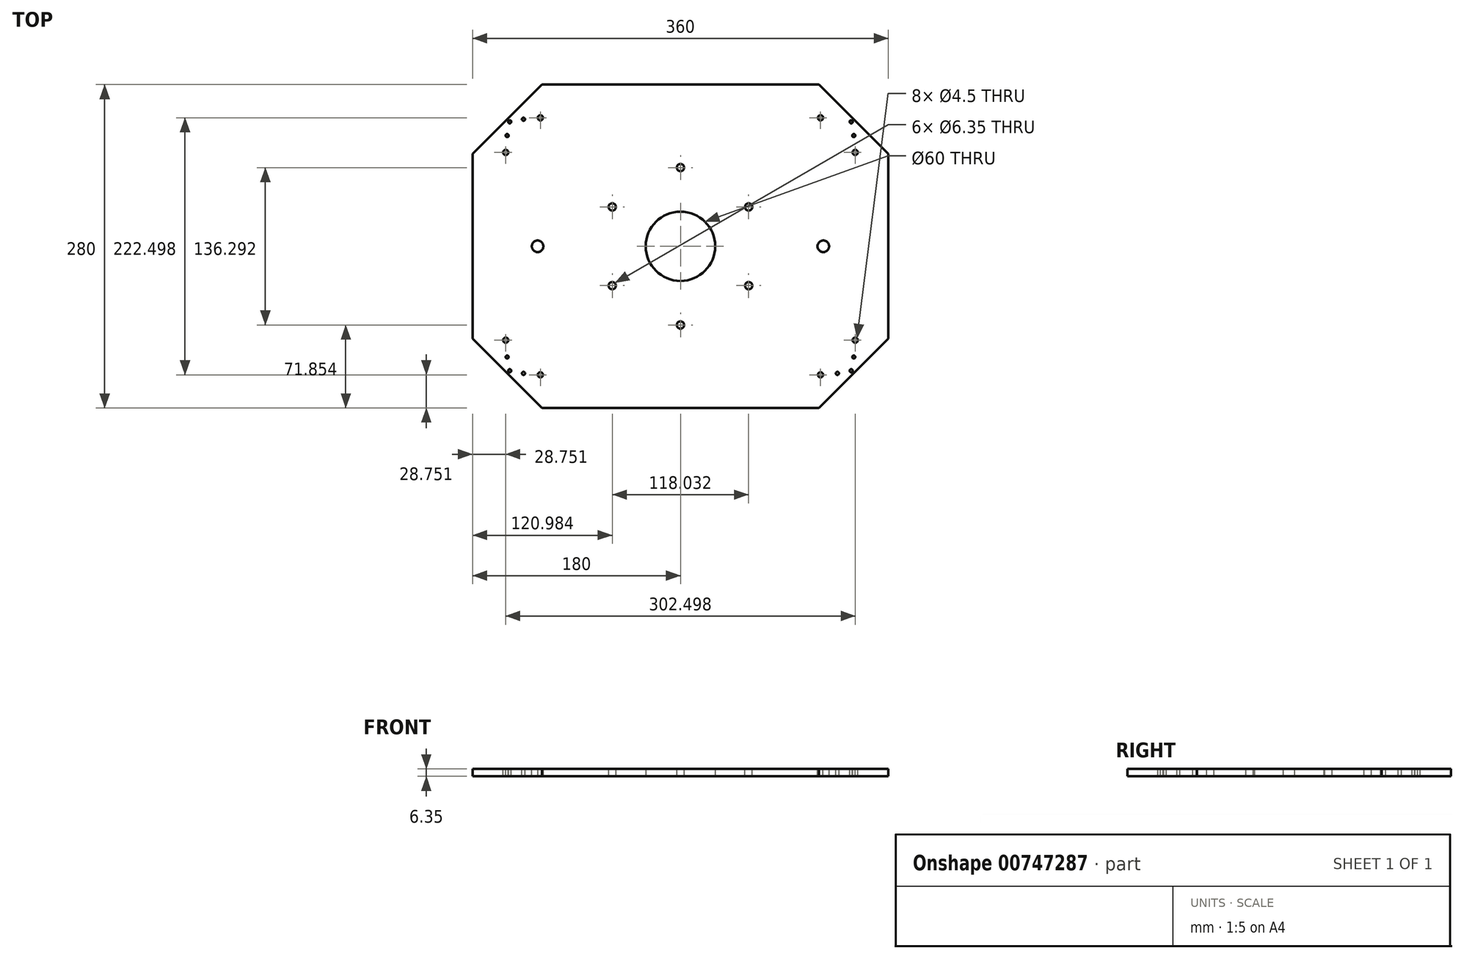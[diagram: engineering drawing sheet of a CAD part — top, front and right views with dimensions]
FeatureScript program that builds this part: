
annotation { "Feature Type Name" : "Feature", "Feature Type Description" : "" }
export const myFeature = defineFeature(function(context is Context, id is Id, definition is map)
    precondition{}
    {
        {
            var Q0;
            Q0=qCreatedBy(makeId("Top.planeOp"),FACE);
            var sketch = newSketch(context, id + "F0", { "sketchPlane" : qUnion([Q0])});
            skLineSegment(sketch, "E0", {"start": v(-120, 0) * mm, "end": v(-180, 60) * mm});
            skLineSegment(sketch, "E1", {"start": v(-180, 60) * mm, "end": v(-180, 220) * mm});
            skLineSegment(sketch, "E2", {"start": v(-180, 220) * mm, "end": v(-120, 280) * mm});
            skLineSegment(sketch, "E3", {"start": v(-120, 280) * mm, "end": v(120, 280) * mm});
            skLineSegment(sketch, "E4", {"start": v(120, 280) * mm, "end": v(180, 220) * mm});
            skLineSegment(sketch, "E5", {"start": v(180, 220) * mm, "end": v(180, 60) * mm});
            skLineSegment(sketch, "E6", {"start": v(180, 60) * mm, "end": v(120, 0) * mm});
            skLineSegment(sketch, "E7", {"start": v(120, 0) * mm, "end": v(-120, 0) * mm});
            skPoint(sketch, "E8.endSnap0", {"position": v(0, 280) * mm});
            skPoint(sketch, "E9.0.midPoint", {"position": v(0, 204.86) * mm});
            skPoint(sketch, "E10.0.midPoint", {"position": v(30.27, 157.38) * mm});
            skLineSegment(sketch, "E11", {"start": v(-180, 140) * mm, "end": v(180, 140) * mm, "construction": true});
            skLineSegment(sketch, "E12", {"start": v(0, 280) * mm, "end": v(0, 0) * mm, "construction": true});
            skCircle(sketch, "E13", {"center": v(0, 140) * mm, "radius": 30 * mm});
            skSolve(sketch);
        }
        {
            var Q0;
            Q0=qSketchRegion(id+"F0",true);
            extrude(context, id + "F1", {"entities" : qUnion([Q0]), "depth" : 6.35 * mm, "offsetDistance" : 25 * mm});
        }
        {
            var Q0;
            {var subQ0=sQuery(id+"F0.wireOp",EDGE,"E2");var subQ1=sQuery(id+"F0.wireOp",EDGE,"E1");var subQ2=sQuery(id+"F0.wireOp",EDGE,"E3");var subQ3=sQuery(id+"F0.wireOp",EDGE,"E0");var subQ4=sQuery(id+"F0.wireOp",EDGE,"E4");var subQ5=sQuery(id+"F0.wireOp",EDGE,"E5");var subQ6=sQuery(id+"F0.wireOp",EDGE,"E6");var subQ7=sQuery(id+"F0.wireOp",EDGE,"E7");Q0=makeQuery(id+"FAH0EIdtt6uSNSP_1.boolean.opBoolean","SPLIT",FACE,{"disambiguationData":[TD([makeQuery(id+"F1.opExtrude","SWEPT_FACE",FACE,{"disambiguationData":[OSD([subQ3])]})])],"derivedFrom":makeQuery(id+"F1.opExtrude","CAP_FACE",FACE,{"disambiguationData":[OSD([subQ3,subQ1,subQ0,subQ2,subQ4,subQ5,subQ6,subQ7,sQuery(id+"F0.wireOp",EDGE,"E10.0"),sQuery(id+"F0.wireOp",EDGE,"E10.1"),sQuery(id+"F0.wireOp",EDGE,"E10.2"),sQuery(id+"F0.wireOp",EDGE,"E10.3"),sQuery(id+"F0.wireOp",EDGE,"E10.4"),sQuery(id+"F0.wireOp",EDGE,"E10.5")])],"isStart":false})});}
            var sketch = newSketch(context, id + "F2", { "sketchPlane" : qUnion([Q0])});
            skLineSegment(sketch, "E14", {"start": v(-180, 140) * mm, "end": v(180, 140) * mm, "construction": true});
            skPoint(sketch, "E15", {"position": v(0, 140) * mm});
            skPoint(sketch, "E16", {"position": v(-123.65, 140) * mm});
            skPoint(sketch, "E17", {"position": v(123.65, 140) * mm});
            skSolve(sketch);
        }
        {
            var Q0;
            Q0=sQuery(id+"F2.wireOp",VERTEX,"E16");
            var Q1;
            Q1=sQuery(id+"F2.wireOp",VERTEX,"E17");
            var Q2;
            Q2=makeQuery(id+"F1.opExtrude","SWEPT_BODY",BODY,{"disambiguationData":[OSD([sQuery(id+"F0.wireOp",EDGE,"E0"),sQuery(id+"F0.wireOp",EDGE,"E1"),sQuery(id+"F0.wireOp",EDGE,"E2"),sQuery(id+"F0.wireOp",EDGE,"E3"),sQuery(id+"F0.wireOp",EDGE,"E4"),sQuery(id+"F0.wireOp",EDGE,"E5"),sQuery(id+"F0.wireOp",EDGE,"E6"),sQuery(id+"F0.wireOp",EDGE,"E7"),sQuery(id+"F0.wireOp",EDGE,"E10.0"),sQuery(id+"F0.wireOp",EDGE,"E10.1"),sQuery(id+"F0.wireOp",EDGE,"E10.2"),sQuery(id+"F0.wireOp",EDGE,"E10.3"),sQuery(id+"F0.wireOp",EDGE,"E10.4"),sQuery(id+"F0.wireOp",EDGE,"E10.5")])]});
            hole(context, id + "F3", {"style" : HoleStyle.SIMPLE, "endStyle" : HoleEndStyle.THROUGH, "holeDiameter" : 10 * mm, "majorDiameter" : 3.17 * mm, "isTappedThrough" : true, "tappedDepth" : 12 * mm, "tapClearance" : 3, "locations" : qUnion([Q0, Q1]), "scope" : qUnion([Q2])});
        }
        {
            var Q0;
            {var subQ0=sQuery(id+"F0.wireOp",EDGE,"E2");var subQ1=sQuery(id+"F0.wireOp",EDGE,"E1");var subQ2=sQuery(id+"F0.wireOp",EDGE,"E3");var subQ3=sQuery(id+"F0.wireOp",EDGE,"E0");var subQ4=sQuery(id+"F0.wireOp",EDGE,"E4");var subQ5=sQuery(id+"F0.wireOp",EDGE,"E5");var subQ6=sQuery(id+"F0.wireOp",EDGE,"E6");var subQ7=sQuery(id+"F0.wireOp",EDGE,"E7");Q0=makeQuery(id+"FAH0EIdtt6uSNSP_1.boolean.opBoolean","SPLIT",FACE,{"disambiguationData":[TD([makeQuery(id+"F1.opExtrude","SWEPT_FACE",FACE,{"disambiguationData":[OSD([subQ3])]})])],"derivedFrom":makeQuery(id+"F1.opExtrude","CAP_FACE",FACE,{"disambiguationData":[OSD([subQ3,subQ1,subQ0,subQ2,subQ4,subQ5,subQ6,subQ7,sQuery(id+"F0.wireOp",EDGE,"E10.0"),sQuery(id+"F0.wireOp",EDGE,"E10.1"),sQuery(id+"F0.wireOp",EDGE,"E10.2"),sQuery(id+"F0.wireOp",EDGE,"E10.3"),sQuery(id+"F0.wireOp",EDGE,"E10.4"),sQuery(id+"F0.wireOp",EDGE,"E10.5")])],"isStart":false})});}
            var sketch = newSketch(context, id + "F4", { "sketchPlane" : qUnion([Q0])});
            skLineSegment(sketch, "E18", {"start": v(-150, 250) * mm, "end": v(-180, 220) * mm, "construction": true});
            skLineSegment(sketch, "E19", {"start": v(-180, 220) * mm, "end": v(-165, 235) * mm, "construction": true});
            skLineSegment(sketch, "E20", {"start": v(-165, 235) * mm, "end": v(-151.25, 221.25) * mm, "construction": true});
            skLineSegment(sketch, "E21", {"start": v(-150, 250) * mm, "end": v(-120, 280) * mm, "construction": true});
            skLineSegment(sketch, "E22", {"start": v(-120, 280) * mm, "end": v(-135, 265) * mm, "construction": true});
            skLineSegment(sketch, "E23", {"start": v(-135, 265) * mm, "end": v(-121.25, 251.25) * mm, "construction": true});
            skLineSegment(sketch, "E24", {"start": v(-150, 30) * mm, "end": v(-180, 60) * mm, "construction": true});
            skLineSegment(sketch, "E25", {"start": v(-180, 60) * mm, "end": v(-165, 45) * mm, "construction": true});
            skLineSegment(sketch, "E26", {"start": v(-165, 45) * mm, "end": v(-151.25, 58.75) * mm, "construction": true});
            skLineSegment(sketch, "E27", {"start": v(-150, 30) * mm, "end": v(-120, 0) * mm, "construction": true});
            skLineSegment(sketch, "E28", {"start": v(-120, 0) * mm, "end": v(-135, 15) * mm, "construction": true});
            skLineSegment(sketch, "E29", {"start": v(-135, 15) * mm, "end": v(-121.25, 28.75) * mm, "construction": true});
            skLineSegment(sketch, "E30", {"start": v(0, 280) * mm, "end": v(0, 0) * mm, "construction": true});
            skLineSegment(sketch, "E31.MirrorCS", {"start": v(135, 265) * mm, "end": v(121.25, 251.25) * mm, "construction": true});
            skLineSegment(sketch, "E32.MirrorCS", {"start": v(165, 235) * mm, "end": v(151.25, 221.25) * mm, "construction": true});
            skLineSegment(sketch, "E33.MirrorCS", {"start": v(165, 45) * mm, "end": v(151.25, 58.75) * mm, "construction": true});
            skLineSegment(sketch, "E34.MirrorCS", {"start": v(135, 15) * mm, "end": v(121.25, 28.75) * mm, "construction": true});
            skLineSegment(sketch, "E35", {"start": v(-180, 220) * mm, "end": v(-175.5, 215.5) * mm, "construction": true});
            skLineSegment(sketch, "E36", {"start": v(-120, 280) * mm, "end": v(-115.5, 275.5) * mm, "construction": true});
            skLineSegment(sketch, "E37", {"start": v(-142.93, 242.93) * mm, "end": v(-135.86, 250) * mm, "construction": true});
            skLineSegment(sketch, "E38", {"start": v(-142.93, 242.93) * mm, "end": v(-150, 235.86) * mm, "construction": true});
            skLineSegment(sketch, "E39.MirrorCS", {"start": v(142.93, 242.93) * mm, "end": v(150, 235.86) * mm, "construction": true});
            skLineSegment(sketch, "E40.MirrorCS", {"start": v(142.93, 242.93) * mm, "end": v(135.86, 250) * mm, "construction": true});
            skLineSegment(sketch, "E41", {"start": v(-180, 140) * mm, "end": v(180, 140) * mm, "construction": true});
            skLineSegment(sketch, "E42.MirrorCS", {"start": v(142.93, 37.07) * mm, "end": v(135.86, 30) * mm, "construction": true});
            skLineSegment(sketch, "E43.MirrorCS", {"start": v(142.93, 37.07) * mm, "end": v(150, 44.14) * mm, "construction": true});
            skLineSegment(sketch, "E44.MirrorCS", {"start": v(-142.93, 37.07) * mm, "end": v(-135.86, 30) * mm, "construction": true});
            skLineSegment(sketch, "E45.MirrorCS", {"start": v(-142.93, 37.07) * mm, "end": v(-150, 44.14) * mm, "construction": true});
            skLineSegment(sketch, "E46", {"start": v(180, 140) * mm, "end": v(180, 101.32) * mm, "construction": true});
            skLineSegment(sketch, "E47", {"start": v(180, 140) * mm, "end": v(180, 178.68) * mm, "construction": true});
            skLineSegment(sketch, "E48", {"start": v(180, 101.32) * mm, "end": v(176.82, 101.32) * mm, "construction": true});
            skLineSegment(sketch, "E49", {"start": v(180, 178.68) * mm, "end": v(176.82, 178.68) * mm, "construction": true});
            skLineSegment(sketch, "E50", {"start": v(180, 140) * mm, "end": v(180, 81.97) * mm, "construction": true});
            skLineSegment(sketch, "E51", {"start": v(180, 81.97) * mm, "end": v(176.82, 81.97) * mm, "construction": true});
            skLineSegment(sketch, "E52", {"start": v(180, 140) * mm, "end": v(180, 198.03) * mm, "construction": true});
            skLineSegment(sketch, "E53", {"start": v(180, 198.03) * mm, "end": v(176.82, 198.03) * mm, "construction": true});
            skLineSegment(sketch, "E54.MirrorCS", {"start": v(-180, 198.03) * mm, "end": v(-176.82, 198.03) * mm, "construction": true});
            skLineSegment(sketch, "E55.MirrorCS", {"start": v(-180, 178.68) * mm, "end": v(-176.82, 178.68) * mm, "construction": true});
            skLineSegment(sketch, "E56.MirrorCS", {"start": v(-180, 101.32) * mm, "end": v(-176.82, 101.32) * mm, "construction": true});
            skLineSegment(sketch, "E57.MirrorCS", {"start": v(-180, 81.97) * mm, "end": v(-176.82, 81.97) * mm, "construction": true});
            skLineSegment(sketch, "E58", {"start": v(-150, 250) * mm, "end": v(-147.75, 247.75) * mm, "construction": true});
            skLineSegment(sketch, "E59", {"start": v(-150, 30) * mm, "end": v(-147.75, 32.25) * mm, "construction": true});
            skLineSegment(sketch, "E60", {"start": v(150, 30) * mm, "end": v(147.75, 32.25) * mm, "construction": true});
            skLineSegment(sketch, "E61", {"start": v(150, 250) * mm, "end": v(147.75, 247.75) * mm, "construction": true});
            skSolve(sketch);
        }
        {
            var Q0;
            Q0=sQuery(id+"F4.wireOp",VERTEX,"E23.end");
            var Q1;
            Q1=sQuery(id+"F4.wireOp",VERTEX,"E20.end");
            var Q2;
            Q2=sQuery(id+"F4.wireOp",VERTEX,"E26.end");
            var Q3;
            Q3=sQuery(id+"F4.wireOp",VERTEX,"E29.end");
            var Q4;
            Q4=sQuery(id+"F4.wireOp",VERTEX,"E34.MirrorCS.end");
            var Q5;
            Q5=sQuery(id+"F4.wireOp",VERTEX,"E33.MirrorCS.end");
            var Q6;
            Q6=sQuery(id+"F4.wireOp",VERTEX,"E32.MirrorCS.end");
            var Q7;
            Q7=sQuery(id+"F4.wireOp",VERTEX,"E31.MirrorCS.end");
            var Q8;
            Q8=makeQuery(id+"F1.opExtrude","SWEPT_BODY",BODY,{"disambiguationData":[OSD([sQuery(id+"F0.wireOp",EDGE,"E0"),sQuery(id+"F0.wireOp",EDGE,"E1"),sQuery(id+"F0.wireOp",EDGE,"E2"),sQuery(id+"F0.wireOp",EDGE,"E3"),sQuery(id+"F0.wireOp",EDGE,"E4"),sQuery(id+"F0.wireOp",EDGE,"E5"),sQuery(id+"F0.wireOp",EDGE,"E6"),sQuery(id+"F0.wireOp",EDGE,"E7"),sQuery(id+"F0.wireOp",EDGE,"E10.0"),sQuery(id+"F0.wireOp",EDGE,"E10.1"),sQuery(id+"F0.wireOp",EDGE,"E10.2"),sQuery(id+"F0.wireOp",EDGE,"E10.3"),sQuery(id+"F0.wireOp",EDGE,"E10.4"),sQuery(id+"F0.wireOp",EDGE,"E10.5")])]});
            hole(context, id + "F5", {"style" : HoleStyle.SIMPLE, "endStyle" : HoleEndStyle.THROUGH, "holeDiameter" : 4.5 * mm, "majorDiameter" : 5 * mm, "isTappedThrough" : true, "tappedDepth" : 12 * mm, "tapClearance" : 3, "locations" : qUnion([Q0, Q1, Q2, Q3, Q4, Q5, Q6, Q7]), "scope" : qUnion([Q8])});
        }
        {
            var Q0;
            Q0=sQuery(id+"F4.wireOp",VERTEX,"E38.end");
            var Q1;
            Q1=sQuery(id+"F4.wireOp",VERTEX,"E37.end");
            var Q2;
            Q2=makeQuery(id+"F1.opExtrude","SWEPT_BODY",BODY,{"disambiguationData":[OSD([sQuery(id+"F0.wireOp",EDGE,"E0"),sQuery(id+"F0.wireOp",EDGE,"E1"),sQuery(id+"F0.wireOp",EDGE,"E2"),sQuery(id+"F0.wireOp",EDGE,"E3"),sQuery(id+"F0.wireOp",EDGE,"E4"),sQuery(id+"F0.wireOp",EDGE,"E5"),sQuery(id+"F0.wireOp",EDGE,"E6"),sQuery(id+"F0.wireOp",EDGE,"E7"),sQuery(id+"F0.wireOp",EDGE,"E13")])]});
            hole(context, id + "F6", {"style" : HoleStyle.SIMPLE, "endStyle" : HoleEndStyle.THROUGH, "standardTappedOrClearance" : lookupTablePath({ "standard" : "ANSI", "engagement" : "75%", "pitch" : "32 tpi", "size" : "#6", "type" : "Tapped" }), "standardBlindInLast" : lookupTablePath({ "standard" : "ANSI", "engagement" : "75%", "pitch" : "32 tpi", "size" : "#6", "type" : "Tapped" }), "holeDiameter" : 2.7 * mm, "majorDiameter" : 3.5 * mm, "showTappedDepth" : true, "isTappedThrough" : true, "tappedDepth" : 12 * mm, "tapClearance" : 3, "locations" : qUnion([Q0, Q1]), "scope" : qUnion([Q2])});
        }
        {
            var Q0;
            Q0=sQuery(id+"F4.wireOp",VERTEX,"E45.MirrorCS.end");
            var Q1;
            Q1=sQuery(id+"F4.wireOp",VERTEX,"E44.MirrorCS.end");
            var Q2;
            Q2=sQuery(id+"F4.wireOp",VERTEX,"E40.MirrorCS.end");
            var Q3;
            Q3=sQuery(id+"F4.wireOp",VERTEX,"E39.MirrorCS.end");
            var Q4;
            Q4=sQuery(id+"F4.wireOp",VERTEX,"E42.MirrorCS.end");
            var Q5;
            Q5=sQuery(id+"F4.wireOp",VERTEX,"E43.MirrorCS.end");
            var Q6;
            Q6=makeQuery(id+"F1.opExtrude","SWEPT_BODY",BODY,{"disambiguationData":[OSD([sQuery(id+"F0.wireOp",EDGE,"E0"),sQuery(id+"F0.wireOp",EDGE,"E1"),sQuery(id+"F0.wireOp",EDGE,"E2"),sQuery(id+"F0.wireOp",EDGE,"E3"),sQuery(id+"F0.wireOp",EDGE,"E4"),sQuery(id+"F0.wireOp",EDGE,"E5"),sQuery(id+"F0.wireOp",EDGE,"E6"),sQuery(id+"F0.wireOp",EDGE,"E7"),sQuery(id+"F0.wireOp",EDGE,"E13")])]});
            hole(context, id + "F7", {"style" : HoleStyle.SIMPLE, "endStyle" : HoleEndStyle.THROUGH, "standardTappedOrClearance" : lookupTablePath({ "standard" : "ANSI", "engagement" : "75%", "pitch" : "32 tpi", "size" : "#6", "type" : "Tapped" }), "standardBlindInLast" : lookupTablePath({ "standard" : "ANSI", "engagement" : "75%", "pitch" : "32 tpi", "size" : "#6", "type" : "Tapped" }), "holeDiameter" : 2.7 * mm, "majorDiameter" : 3.5 * mm, "showTappedDepth" : true, "isTappedThrough" : true, "tappedDepth" : 12 * mm, "tapClearance" : 3, "locations" : qUnion([Q0, Q1, Q2, Q3, Q4, Q5]), "scope" : qUnion([Q6])});
        }
        {
            var Q0;
            Q0=makeQuery(id+"F4.imprint","IMPRINT",FACE,{"disambiguationData":[TD([[makeQuery(id+"F4.imprint","IMPRINT",EDGE,{"derivedFrom":makeQuery(id+"F1.opExtrude","CAP_EDGE",EDGE,{"disambiguationData":[OSD([sQuery(id+"F0.wireOp",EDGE,"E0")])],"isStart":false})}),-1.0]])]});
            var sketch = newSketch(context, id + "F8", { "sketchPlane" : qUnion([Q0])});
            skCircle(sketch, "E62.cCircle", {"center": v(0, 140) * mm, "radius": 59.02 * mm, "construction": true});
            skLineSegment(sketch, "E62.0", {"start": v(0, 208.15) * mm, "end": v(59.02, 174.07) * mm});
            skLineSegment(sketch, "E62.1", {"start": v(59.02, 174.07) * mm, "end": v(59.02, 105.93) * mm});
            skLineSegment(sketch, "E62.2", {"start": v(59.02, 105.93) * mm, "end": v(0, 71.85) * mm});
            skLineSegment(sketch, "E62.3", {"start": v(0, 71.85) * mm, "end": v(-59.02, 105.93) * mm});
            skLineSegment(sketch, "E62.4", {"start": v(-59.02, 105.93) * mm, "end": v(-59.02, 174.07) * mm});
            skLineSegment(sketch, "E62.5", {"start": v(-59.02, 174.07) * mm, "end": v(0, 208.15) * mm});
            skPoint(sketch, "E62.0.midPoint", {"position": v(29.5, 191.1) * mm});
            skSolve(sketch);
        }
        {
            var Q0;
            Q0=sQuery(id+"F8.wireOp",VERTEX,"E62.5.end");
            var Q1;
            Q1=sQuery(id+"F8.wireOp",VERTEX,"E62.0.end");
            var Q2;
            Q2=sQuery(id+"F8.wireOp",VERTEX,"E62.5.start");
            var Q3;
            Q3=sQuery(id+"F8.wireOp",VERTEX,"E62.4.start");
            var Q4;
            Q4=sQuery(id+"F8.wireOp",VERTEX,"E62.2.end");
            var Q5;
            Q5=sQuery(id+"F8.wireOp",VERTEX,"E62.1.end");
            var Q6;
            Q6=makeQuery(id+"F1.opExtrude","SWEPT_BODY",BODY,{"disambiguationData":[OSD([sQuery(id+"F0.wireOp",EDGE,"E0"),sQuery(id+"F0.wireOp",EDGE,"E1"),sQuery(id+"F0.wireOp",EDGE,"E2"),sQuery(id+"F0.wireOp",EDGE,"E3"),sQuery(id+"F0.wireOp",EDGE,"E4"),sQuery(id+"F0.wireOp",EDGE,"E5"),sQuery(id+"F0.wireOp",EDGE,"E6"),sQuery(id+"F0.wireOp",EDGE,"E7"),sQuery(id+"F0.wireOp",EDGE,"E13")])]});
            hole(context, id + "F9", {"style" : HoleStyle.SIMPLE, "endStyle" : HoleEndStyle.THROUGH, "holeDiameter" : 6.35 * mm, "majorDiameter" : 3 * mm, "isTappedThrough" : true, "tappedDepth" : 12 * mm, "tapClearance" : 3, "locations" : qUnion([Q0, Q1, Q2, Q3, Q4, Q5]), "scope" : qUnion([Q6])});
        }
        {
            var Q0;
            Q0=sQuery(id+"F4.wireOp",VERTEX,"E61.end");
            var Q1;
            Q1=sQuery(id+"F4.wireOp",VERTEX,"E60.end");
            var Q2;
            Q2=sQuery(id+"F4.wireOp",VERTEX,"E59.end");
            var Q3;
            Q3=sQuery(id+"F4.wireOp",VERTEX,"E58.end");
            var Q4;
            Q4=makeQuery(id+"F1.opExtrude","SWEPT_BODY",BODY,{"disambiguationData":[OSD([sQuery(id+"F0.wireOp",EDGE,"E0"),sQuery(id+"F0.wireOp",EDGE,"E1"),sQuery(id+"F0.wireOp",EDGE,"E2"),sQuery(id+"F0.wireOp",EDGE,"E3"),sQuery(id+"F0.wireOp",EDGE,"E4"),sQuery(id+"F0.wireOp",EDGE,"E5"),sQuery(id+"F0.wireOp",EDGE,"E6"),sQuery(id+"F0.wireOp",EDGE,"E7"),sQuery(id+"F0.wireOp",EDGE,"E13")])]});
            hole(context, id + "F10", {"style" : HoleStyle.SIMPLE, "endStyle" : HoleEndStyle.THROUGH, "standardTappedOrClearance" : lookupTablePath({ "standard" : "ANSI", "engagement" : "75%", "pitch" : "32 tpi", "size" : "#6", "type" : "Tapped" }), "standardBlindInLast" : lookupTablePath({ "standard" : "ANSI", "engagement" : "75%", "pitch" : "32 tpi", "size" : "#6", "type" : "Tapped" }), "holeDiameter" : 2.7 * mm, "majorDiameter" : 3.5 * mm, "showTappedDepth" : true, "isTappedThrough" : true, "tappedDepth" : 12 * mm, "tapClearance" : 3, "locations" : qUnion([Q0, Q1, Q2, Q3]), "scope" : qUnion([Q4])});
        }
    });
